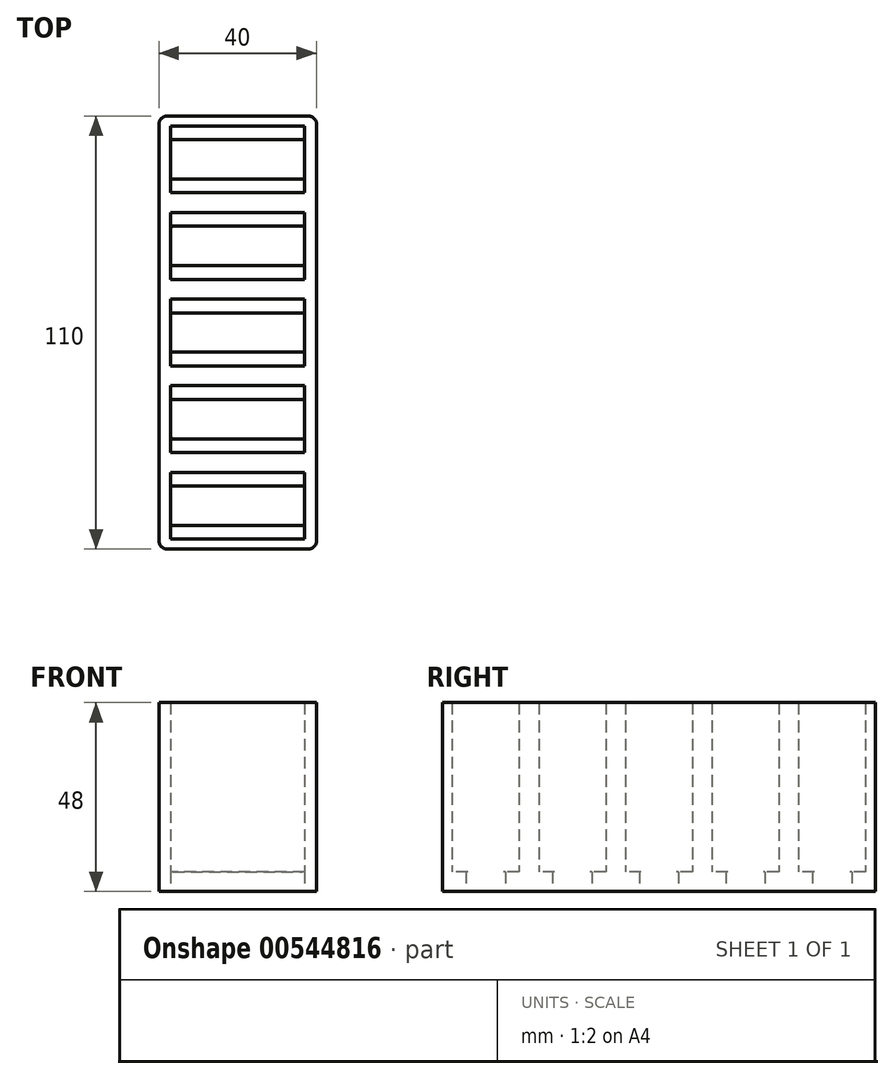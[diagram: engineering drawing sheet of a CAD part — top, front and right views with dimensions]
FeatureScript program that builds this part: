
annotation { "Feature Type Name" : "Feature", "Feature Type Description" : "" }
export const myFeature = defineFeature(function(context is Context, id is Id, definition is map)
    precondition{}
    {
        {
            var Q0;
            Q0=qCreatedBy(makeId("Top.planeOp"),FACE);
            var sketch = newSketch(context, id + "F0", { "sketchPlane" : qUnion([Q0])});
            skLineSegment(sketch, "E0.bottom", {"start": v(2, 0) * mm, "end": v(38, 0) * mm});
            skLineSegment(sketch, "E0.top", {"start": v(2, 110) * mm, "end": v(38, 110) * mm});
            skLineSegment(sketch, "E0.left", {"start": v(0, 2) * mm, "end": v(0, 108) * mm});
            skLineSegment(sketch, "E0.right", {"start": v(40, 2) * mm, "end": v(40, 108) * mm});
            skLineSegment(sketch, "E1.0", {"start": v(3, 0) * mm, "end": v(3, 110) * mm, "construction": true});
            skLineSegment(sketch, "E2.0", {"start": v(0, 2.5) * mm, "end": v(40, 2.5) * mm, "construction": true});
            skLineSegment(sketch, "E3.bottom", {"start": v(3, 2.5) * mm, "end": v(37, 2.5) * mm});
            skLineSegment(sketch, "E3.top", {"start": v(3, 19.5) * mm, "end": v(37, 19.5) * mm});
            skLineSegment(sketch, "E3.left", {"start": v(3, 2.5) * mm, "end": v(3, 19.5) * mm});
            skLineSegment(sketch, "E3.right", {"start": v(37, 2.5) * mm, "end": v(37, 19.5) * mm});
            skLineSegment(sketch, "E4.0", {"start": v(3, 16) * mm, "end": v(37, 16) * mm});
            skLineSegment(sketch, "E5.0", {"start": v(3, 6) * mm, "end": v(37, 6) * mm});
            skLineSegment(sketch, "E6.0.1.0", {"start": v(3, 41.5) * mm, "end": v(37, 41.5) * mm});
            skLineSegment(sketch, "E6.0.1.1", {"start": v(37, 24.5) * mm, "end": v(37, 41.5) * mm});
            skLineSegment(sketch, "E6.0.1.2", {"start": v(3, 24.5) * mm, "end": v(37, 24.5) * mm});
            skLineSegment(sketch, "E6.0.1.3", {"start": v(3, 24.5) * mm, "end": v(3, 41.5) * mm});
            skLineSegment(sketch, "E6.0.1.4", {"start": v(3, 38) * mm, "end": v(37, 38) * mm});
            skLineSegment(sketch, "E6.0.1.5", {"start": v(3, 28) * mm, "end": v(37, 28) * mm});
            skLineSegment(sketch, "E6.0.2.0", {"start": v(3, 63.5) * mm, "end": v(37, 63.5) * mm});
            skLineSegment(sketch, "E6.0.2.1", {"start": v(37, 46.5) * mm, "end": v(37, 63.5) * mm});
            skLineSegment(sketch, "E6.0.2.2", {"start": v(3, 46.5) * mm, "end": v(37, 46.5) * mm});
            skLineSegment(sketch, "E6.0.2.3", {"start": v(3, 46.5) * mm, "end": v(3, 63.5) * mm});
            skLineSegment(sketch, "E6.0.2.4", {"start": v(3, 60) * mm, "end": v(37, 60) * mm});
            skLineSegment(sketch, "E6.0.2.5", {"start": v(3, 50) * mm, "end": v(37, 50) * mm});
            skLineSegment(sketch, "E6.0.3.0", {"start": v(3, 85.5) * mm, "end": v(37, 85.5) * mm});
            skLineSegment(sketch, "E6.0.3.1", {"start": v(37, 68.5) * mm, "end": v(37, 85.5) * mm});
            skLineSegment(sketch, "E6.0.3.2", {"start": v(3, 68.5) * mm, "end": v(37, 68.5) * mm});
            skLineSegment(sketch, "E6.0.3.3", {"start": v(3, 68.5) * mm, "end": v(3, 85.5) * mm});
            skLineSegment(sketch, "E6.0.3.4", {"start": v(3, 82) * mm, "end": v(37, 82) * mm});
            skLineSegment(sketch, "E6.0.3.5", {"start": v(3, 72) * mm, "end": v(37, 72) * mm});
            skLineSegment(sketch, "E6.0.4.0", {"start": v(3, 107.5) * mm, "end": v(37, 107.5) * mm});
            skLineSegment(sketch, "E6.0.4.1", {"start": v(37, 90.5) * mm, "end": v(37, 107.5) * mm});
            skLineSegment(sketch, "E6.0.4.2", {"start": v(3, 90.5) * mm, "end": v(37, 90.5) * mm});
            skLineSegment(sketch, "E6.0.4.3", {"start": v(3, 90.5) * mm, "end": v(3, 107.5) * mm});
            skLineSegment(sketch, "E6.0.4.4", {"start": v(3, 104) * mm, "end": v(37, 104) * mm});
            skLineSegment(sketch, "E6.0.4.5", {"start": v(3, 94) * mm, "end": v(37, 94) * mm});
            skLineSegment(sketch, "E6.direction1", {"start": v(3, 2.5) * mm, "end": v(28, 2.5) * mm, "construction": true});
            skLineSegment(sketch, "E6.direction2", {"start": v(3, 2.5) * mm, "end": v(3, 24.5) * mm, "construction": true});
            skPoint(sketch, "E7.visualSharp", {"position": v(0, 0) * mm});
            skArc(sketch, "E7.filletArc", {"start": v(0, 2) * mm, "mid": v(0.59, 0.59) * mm, "end": v(2, 0) * mm});
            skPoint(sketch, "E8.visualSharp", {"position": v(0, 110) * mm});
            skArc(sketch, "E8.filletArc", {"start": v(2, 110) * mm, "mid": v(0.59, 109.41) * mm, "end": v(0, 108) * mm});
            skPoint(sketch, "E9.visualSharp", {"position": v(40, 110) * mm});
            skArc(sketch, "E9.filletArc", {"start": v(40, 108) * mm, "mid": v(39.41, 109.41) * mm, "end": v(38, 110) * mm});
            skPoint(sketch, "E10.visualSharp", {"position": v(40, 0) * mm});
            skArc(sketch, "E10.filletArc", {"start": v(38, 0) * mm, "mid": v(39.41, 0.59) * mm, "end": v(40, 2) * mm});
            skSolve(sketch);
        }
        {
            var Q0;
            Q0 = qSketchRegion(id + "F0", true);
            var Q1;
            {var subQ0=sQuery(id+"F0.wireOp",EDGE,"E3.top");Q1=makeQuery(id+"F0.imprint","IMPRINT",FACE,{"disambiguationData":[TD([[makeQuery(id+"F0.imprint","IMPRINT",EDGE,{"derivedFrom":subQ0}),-1.0]])]});}
            var Q2;
            {var subQ0=sQuery(id+"F0.wireOp",EDGE,"E6.0.1.0");Q2=makeQuery(id+"F0.imprint","IMPRINT",FACE,{"disambiguationData":[TD([[makeQuery(id+"F0.imprint","IMPRINT",EDGE,{"derivedFrom":subQ0}),-1.0]])]});}
            var Q3;
            {var subQ0=sQuery(id+"F0.wireOp",EDGE,"E6.0.2.0");Q3=makeQuery(id+"F0.imprint","IMPRINT",FACE,{"disambiguationData":[TD([[makeQuery(id+"F0.imprint","IMPRINT",EDGE,{"derivedFrom":subQ0}),-1.0]])]});}
            var Q4;
            {var subQ0=sQuery(id+"F0.wireOp",EDGE,"E6.0.3.0");Q4=makeQuery(id+"F0.imprint","IMPRINT",FACE,{"disambiguationData":[TD([[makeQuery(id+"F0.imprint","IMPRINT",EDGE,{"derivedFrom":subQ0}),-1.0]])]});}
            var Q5;
            {var subQ0=sQuery(id+"F0.wireOp",EDGE,"E6.0.4.0");Q5=makeQuery(id+"F0.imprint","IMPRINT",FACE,{"disambiguationData":[TD([[makeQuery(id+"F0.imprint","IMPRINT",EDGE,{"derivedFrom":subQ0}),-1.0]])]});}
            var Q6;
            {var subQ0=sQuery(id+"F0.wireOp",EDGE,"E6.0.4.2");Q6=makeQuery(id+"F0.imprint","IMPRINT",FACE,{"disambiguationData":[TD([[makeQuery(id+"F0.imprint","IMPRINT",EDGE,{"derivedFrom":subQ0}),1.0]])]});}
            var Q7;
            {var subQ0=sQuery(id+"F0.wireOp",EDGE,"E6.0.3.2");Q7=makeQuery(id+"F0.imprint","IMPRINT",FACE,{"disambiguationData":[TD([[makeQuery(id+"F0.imprint","IMPRINT",EDGE,{"derivedFrom":subQ0}),1.0]])]});}
            var Q8;
            {var subQ0=sQuery(id+"F0.wireOp",EDGE,"E6.0.2.2");Q8=makeQuery(id+"F0.imprint","IMPRINT",FACE,{"disambiguationData":[TD([[makeQuery(id+"F0.imprint","IMPRINT",EDGE,{"derivedFrom":subQ0}),1.0]])]});}
            var Q9;
            {var subQ0=sQuery(id+"F0.wireOp",EDGE,"E6.0.1.2");Q9=makeQuery(id+"F0.imprint","IMPRINT",FACE,{"disambiguationData":[TD([[makeQuery(id+"F0.imprint","IMPRINT",EDGE,{"derivedFrom":subQ0}),1.0]])]});}
            var Q10;
            {var subQ0=sQuery(id+"F0.wireOp",EDGE,"E3.bottom");Q10=makeQuery(id+"F0.imprint","IMPRINT",FACE,{"disambiguationData":[TD([[makeQuery(id+"F0.imprint","IMPRINT",EDGE,{"derivedFrom":subQ0}),1.0]])]});}
            extrude(context, id + "F1", {"entities" : qUnion([Q0, Q1, Q2, Q3, Q4, Q5, Q6, Q7, Q8, Q9, Q10]), "depth" : 5 * mm, "offsetDistance" : 25 * mm});
        }
        {
            var Q0;
            Q0=makeQuery(id+"F1.opExtrude","SWEPT_EDGE",EDGE,{"disambiguationData":[OSD([sQuery(id+"F0.wireOp",EDGE,"E6.0.1.3"),sQuery(id+"F0.wireOp",EDGE,"E6.0.1.5")])]});
            var Q1;
            Q1=makeQuery(id+"F1.opExtrude","SWEPT_EDGE",EDGE,{"disambiguationData":[OSD([sQuery(id+"F0.wireOp",EDGE,"E3.left"),sQuery(id+"F0.wireOp",EDGE,"E5.0")])]});
            var Q2;
            Q2=makeQuery(id+"F1.opExtrude","SWEPT_EDGE",EDGE,{"disambiguationData":[OSD([sQuery(id+"F0.wireOp",EDGE,"E6.0.2.3"),sQuery(id+"F0.wireOp",EDGE,"E6.0.2.5")])]});
            var Q3;
            Q3=makeQuery(id+"F1.opExtrude","SWEPT_EDGE",EDGE,{"disambiguationData":[OSD([sQuery(id+"F0.wireOp",EDGE,"E6.0.3.3"),sQuery(id+"F0.wireOp",EDGE,"E6.0.3.5")])]});
            var Q4;
            Q4=makeQuery(id+"F1.opExtrude","SWEPT_EDGE",EDGE,{"disambiguationData":[OSD([sQuery(id+"F0.wireOp",EDGE,"E6.0.4.3"),sQuery(id+"F0.wireOp",EDGE,"E6.0.4.5")])]});
            var Q5;
            Q5=makeQuery(id+"F1.opExtrude","SWEPT_EDGE",EDGE,{"disambiguationData":[OSD([sQuery(id+"F0.wireOp",EDGE,"E6.0.4.3"),sQuery(id+"F0.wireOp",EDGE,"E6.0.4.4")])]});
            var Q6;
            Q6=makeQuery(id+"F1.opExtrude","SWEPT_EDGE",EDGE,{"disambiguationData":[OSD([sQuery(id+"F0.wireOp",EDGE,"E6.0.3.3"),sQuery(id+"F0.wireOp",EDGE,"E6.0.3.4")])]});
            var Q7;
            Q7=makeQuery(id+"F1.opExtrude","SWEPT_EDGE",EDGE,{"disambiguationData":[OSD([sQuery(id+"F0.wireOp",EDGE,"E6.0.2.3"),sQuery(id+"F0.wireOp",EDGE,"E6.0.2.4")])]});
            var Q8;
            Q8=makeQuery(id+"F1.opExtrude","SWEPT_EDGE",EDGE,{"disambiguationData":[OSD([sQuery(id+"F0.wireOp",EDGE,"E6.0.1.3"),sQuery(id+"F0.wireOp",EDGE,"E6.0.1.4")])]});
            var Q9;
            Q9=makeQuery(id+"F1.opExtrude","SWEPT_EDGE",EDGE,{"disambiguationData":[OSD([sQuery(id+"F0.wireOp",EDGE,"E3.left"),sQuery(id+"F0.wireOp",EDGE,"E4.0")])]});
            var Q10;
            Q10=makeQuery(id+"F1.opExtrude","SWEPT_EDGE",EDGE,{"disambiguationData":[OSD([sQuery(id+"F0.wireOp",EDGE,"E6.0.4.1"),sQuery(id+"F0.wireOp",EDGE,"E6.0.4.4")])]});
            var Q11;
            Q11=makeQuery(id+"F1.opExtrude","SWEPT_EDGE",EDGE,{"disambiguationData":[OSD([sQuery(id+"F0.wireOp",EDGE,"E6.0.3.1"),sQuery(id+"F0.wireOp",EDGE,"E6.0.3.4")])]});
            var Q12;
            Q12=makeQuery(id+"F1.opExtrude","SWEPT_EDGE",EDGE,{"disambiguationData":[OSD([sQuery(id+"F0.wireOp",EDGE,"E6.0.2.1"),sQuery(id+"F0.wireOp",EDGE,"E6.0.2.4")])]});
            var Q13;
            Q13=makeQuery(id+"F1.opExtrude","SWEPT_EDGE",EDGE,{"disambiguationData":[OSD([sQuery(id+"F0.wireOp",EDGE,"E6.0.1.1"),sQuery(id+"F0.wireOp",EDGE,"E6.0.1.4")])]});
            var Q14;
            Q14=makeQuery(id+"F1.opExtrude","SWEPT_EDGE",EDGE,{"disambiguationData":[OSD([sQuery(id+"F0.wireOp",EDGE,"E3.right"),sQuery(id+"F0.wireOp",EDGE,"E4.0")])]});
            var Q15;
            Q15=makeQuery(id+"F1.opExtrude","SWEPT_EDGE",EDGE,{"disambiguationData":[OSD([sQuery(id+"F0.wireOp",EDGE,"E3.right"),sQuery(id+"F0.wireOp",EDGE,"E5.0")])]});
            var Q16;
            Q16=makeQuery(id+"F1.opExtrude","SWEPT_EDGE",EDGE,{"disambiguationData":[OSD([sQuery(id+"F0.wireOp",EDGE,"E6.0.1.1"),sQuery(id+"F0.wireOp",EDGE,"E6.0.1.5")])]});
            var Q17;
            Q17=makeQuery(id+"F1.opExtrude","SWEPT_EDGE",EDGE,{"disambiguationData":[OSD([sQuery(id+"F0.wireOp",EDGE,"E6.0.2.1"),sQuery(id+"F0.wireOp",EDGE,"E6.0.2.5")])]});
            var Q18;
            Q18=makeQuery(id+"F1.opExtrude","SWEPT_EDGE",EDGE,{"disambiguationData":[OSD([sQuery(id+"F0.wireOp",EDGE,"E6.0.3.1"),sQuery(id+"F0.wireOp",EDGE,"E6.0.3.5")])]});
            var Q19;
            Q19=makeQuery(id+"F1.opExtrude","SWEPT_EDGE",EDGE,{"disambiguationData":[OSD([sQuery(id+"F0.wireOp",EDGE,"E6.0.4.1"),sQuery(id+"F0.wireOp",EDGE,"E6.0.4.5")])]});
            fillet(context, id + "F2", {"entities" : qUnion([Q0, Q1, Q2, Q3, Q4, Q5, Q6, Q7, Q8, Q9, Q10, Q11, Q12, Q13, Q14, Q15, Q16, Q17, Q18, Q19]), "radius" : 0.5 * mm, "tangentPropagation" : true, "allowEdgeOverflow" : false});
        }
        {
            var Q0;
            Q0 = qSketchRegion(id + "F0", true);
            extrude(context, id + "F3", {"entities" : qUnion([Q0]), "operationType" : NewBodyOperationType.ADD, "depth" : 48 * mm, "offsetDistance" : 25 * mm});
        }
    });
